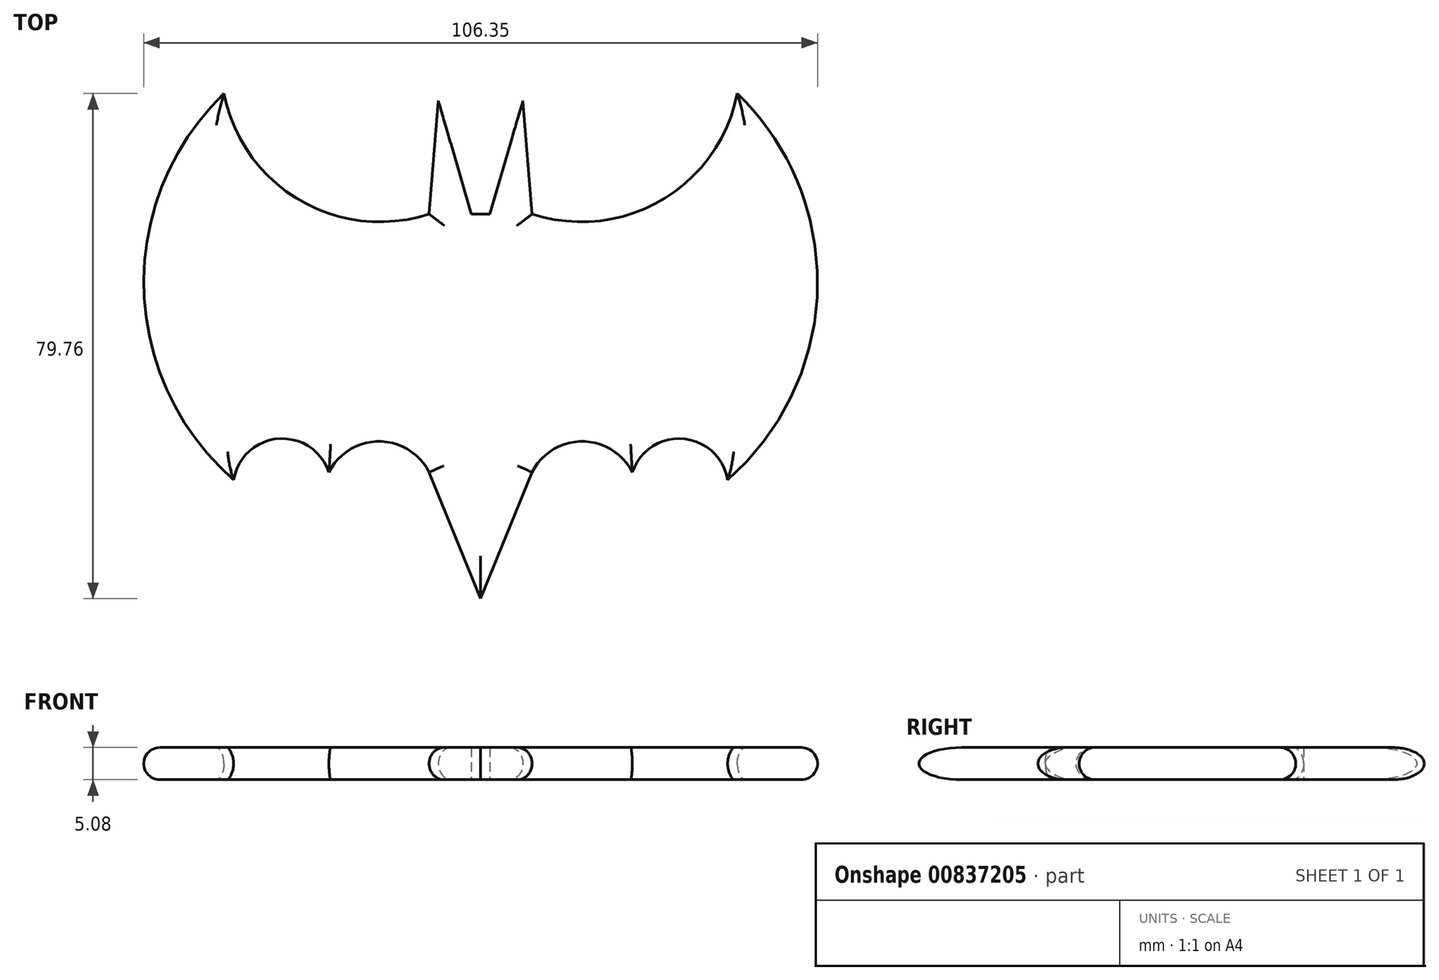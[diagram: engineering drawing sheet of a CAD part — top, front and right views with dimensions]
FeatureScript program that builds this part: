
annotation { "Feature Type Name" : "Feature", "Feature Type Description" : "" }
export const myFeature = defineFeature(function(context is Context, id is Id, definition is map)
    precondition{}
    {
        {
            var Q0;
            Q0=qCreatedBy(makeId("Top.planeOp"),FACE);
            var sketch = newSketch(context, id + "F0", { "sketchPlane" : qUnion([Q0])});
            skLineSegment(sketch, "E0", {"start": v(3.39, 55.96) * mm, "end": v(8.6, 73.82) * mm});
            skLineSegment(sketch, "E1", {"start": v(8.6, 73.82) * mm, "end": v(10.04, 55.96) * mm});
            skArc(sketch, "E2", {"start": v(10.04, 55.96) * mm, "mid": v(30.52, 58.16) * mm, "end": v(42.42, 74.98) * mm});
            skArc(sketch, "E3", {"start": v(40.9, 14) * mm, "mid": v(55.08, 44.16) * mm, "end": v(42.42, 74.98) * mm});
            skArc(sketch, "E4", {"start": v(40.9, 14) * mm, "mid": v(33.84, 20.48) * mm, "end": v(25.86, 15.17) * mm});
            skArc(sketch, "E5", {"start": v(25.86, 15.17) * mm, "mid": v(17.95, 20.06) * mm, "end": v(10.04, 15.17) * mm});
            skLineSegment(sketch, "E6", {"start": v(10.04, 15.17) * mm, "end": v(1.92, -4.78) * mm});
            skLineSegment(sketch, "E7", {"start": v(1.92, -4.78) * mm, "end": v(1.92, 55.96) * mm});
            skLineSegment(sketch, "E8", {"start": v(3.39, 55.96) * mm, "end": v(1.92, 55.96) * mm});
            skArc(sketch, "E9.MirrorCS", {"start": v(-6.2, 55.96) * mm, "mid": v(-26.69, 58.16) * mm, "end": v(-38.58, 74.98) * mm});
            skLineSegment(sketch, "E10.MirrorCS", {"start": v(-4.76, 73.82) * mm, "end": v(-6.2, 55.96) * mm});
            skLineSegment(sketch, "E11.MirrorCS", {"start": v(0.45, 55.96) * mm, "end": v(-4.76, 73.82) * mm});
            skLineSegment(sketch, "E12.MirrorCS", {"start": v(0.45, 55.96) * mm, "end": v(1.92, 55.96) * mm});
            skLineSegment(sketch, "E13.MirrorCS", {"start": v(-6.2, 15.17) * mm, "end": v(1.92, -4.78) * mm});
            skArc(sketch, "E14.MirrorCS", {"start": v(-37.06, 14) * mm, "mid": v(-30, 20.48) * mm, "end": v(-22.03, 15.17) * mm});
            skArc(sketch, "E15.MirrorCS", {"start": v(-22.03, 15.17) * mm, "mid": v(-14.12, 20.06) * mm, "end": v(-6.2, 15.17) * mm});
            skArc(sketch, "E16.MirrorCS", {"start": v(-37.06, 14) * mm, "mid": v(-51.24, 44.16) * mm, "end": v(-38.58, 74.98) * mm});
            skSolve(sketch);
        }
        {
            var Q0;
            Q0 = qSketchRegion(id + "F0", true);
            extrude(context, id + "F1", {"entities" : qUnion([Q0]), "depth" : 5.08 * mm, "offsetDistance" : 25.4 * mm});
        }
        {
            var Q0;
            Q0=makeQuery(id+"F1.opExtrude","CAP_EDGE",EDGE,{"disambiguationData":[OSD([sQuery(id+"F0.wireOp",EDGE,"E1")])],"isStart":true});
            var Q1;
            Q1=makeQuery(id+"F1.opExtrude","CAP_EDGE",EDGE,{"disambiguationData":[OSD([sQuery(id+"F0.wireOp",EDGE,"E1")])],"isStart":false});
            var Q2;
            Q2=makeQuery(id+"F1.opExtrude","CAP_EDGE",EDGE,{"disambiguationData":[OSD([sQuery(id+"F0.wireOp",EDGE,"E10.MirrorCS")])],"isStart":true});
            var Q3;
            Q3=makeQuery(id+"F1.opExtrude","CAP_EDGE",EDGE,{"disambiguationData":[OSD([sQuery(id+"F0.wireOp",EDGE,"E10.MirrorCS")])],"isStart":false});
            var Q4;
            Q4=makeQuery(id+"F1.opExtrude","CAP_EDGE",EDGE,{"disambiguationData":[OSD([sQuery(id+"F0.wireOp",EDGE,"E9.MirrorCS")])],"isStart":false});
            var Q5;
            Q5=makeQuery(id+"F1.opExtrude","CAP_EDGE",EDGE,{"disambiguationData":[OSD([sQuery(id+"F0.wireOp",EDGE,"E9.MirrorCS")])],"isStart":true});
            var Q6;
            Q6=makeQuery(id+"F1.opExtrude","CAP_EDGE",EDGE,{"disambiguationData":[OSD([sQuery(id+"F0.wireOp",EDGE,"E2")])],"isStart":true});
            var Q7;
            Q7=makeQuery(id+"F1.opExtrude","CAP_EDGE",EDGE,{"disambiguationData":[OSD([sQuery(id+"F0.wireOp",EDGE,"E16.MirrorCS")])],"isStart":true});
            var Q8;
            Q8=makeQuery(id+"F1.opExtrude","CAP_EDGE",EDGE,{"disambiguationData":[OSD([sQuery(id+"F0.wireOp",EDGE,"E16.MirrorCS")])],"isStart":false});
            var Q9;
            Q9=makeQuery(id+"F1.opExtrude","CAP_EDGE",EDGE,{"disambiguationData":[OSD([sQuery(id+"F0.wireOp",EDGE,"E3")])],"isStart":true});
            var Q10;
            Q10=makeQuery(id+"F1.opExtrude","CAP_EDGE",EDGE,{"disambiguationData":[OSD([sQuery(id+"F0.wireOp",EDGE,"E3")])],"isStart":false});
            var Q11;
            Q11=makeQuery(id+"F1.opExtrude","CAP_EDGE",EDGE,{"disambiguationData":[OSD([sQuery(id+"F0.wireOp",EDGE,"E4")])],"isStart":true});
            var Q12;
            Q12=makeQuery(id+"F1.opExtrude","CAP_EDGE",EDGE,{"disambiguationData":[OSD([sQuery(id+"F0.wireOp",EDGE,"E14.MirrorCS")])],"isStart":true});
            var Q13;
            Q13=makeQuery(id+"F1.opExtrude","CAP_EDGE",EDGE,{"disambiguationData":[OSD([sQuery(id+"F0.wireOp",EDGE,"E14.MirrorCS")])],"isStart":false});
            var Q14;
            Q14=makeQuery(id+"F1.opExtrude","CAP_EDGE",EDGE,{"disambiguationData":[OSD([sQuery(id+"F0.wireOp",EDGE,"E4")])],"isStart":false});
            var Q15;
            Q15=makeQuery(id+"F1.opExtrude","CAP_EDGE",EDGE,{"disambiguationData":[OSD([sQuery(id+"F0.wireOp",EDGE,"E15.MirrorCS")])],"isStart":false});
            var Q16;
            Q16=makeQuery(id+"F1.opExtrude","CAP_EDGE",EDGE,{"disambiguationData":[OSD([sQuery(id+"F0.wireOp",EDGE,"E5")])],"isStart":false});
            var Q17;
            Q17=makeQuery(id+"F1.opExtrude","CAP_EDGE",EDGE,{"disambiguationData":[OSD([sQuery(id+"F0.wireOp",EDGE,"E5")])],"isStart":true});
            var Q18;
            Q18=makeQuery(id+"F1.opExtrude","CAP_EDGE",EDGE,{"disambiguationData":[OSD([sQuery(id+"F0.wireOp",EDGE,"E15.MirrorCS")])],"isStart":true});
            var Q19;
            Q19=makeQuery(id+"F1.opExtrude","CAP_EDGE",EDGE,{"disambiguationData":[OSD([sQuery(id+"F0.wireOp",EDGE,"E6")])],"isStart":false});
            var Q20;
            Q20=makeQuery(id+"F1.opExtrude","CAP_EDGE",EDGE,{"disambiguationData":[OSD([sQuery(id+"F0.wireOp",EDGE,"E13.MirrorCS")])],"isStart":false});
            var Q21;
            Q21=makeQuery(id+"F1.opExtrude","CAP_EDGE",EDGE,{"disambiguationData":[OSD([sQuery(id+"F0.wireOp",EDGE,"E13.MirrorCS")])],"isStart":true});
            var Q22;
            Q22=makeQuery(id+"F1.opExtrude","CAP_EDGE",EDGE,{"disambiguationData":[OSD([sQuery(id+"F0.wireOp",EDGE,"E6")])],"isStart":true});
            var Q23;
            Q23=makeQuery(id+"F1.opExtrude","CAP_EDGE",EDGE,{"disambiguationData":[OSD([sQuery(id+"F0.wireOp",EDGE,"E2")])],"isStart":false});
            fillet(context, id + "F2", {"entities" : qUnion([Q0, Q1, Q2, Q3, Q4, Q5, Q6, Q7, Q8, Q9, Q10, Q11, Q12, Q13, Q14, Q15, Q16, Q17, Q18, Q19, Q20, Q21, Q22, Q23]), "radius" : 2.54 * mm, "tangentPropagation" : true, "allowEdgeOverflow" : false});
        }
    });
